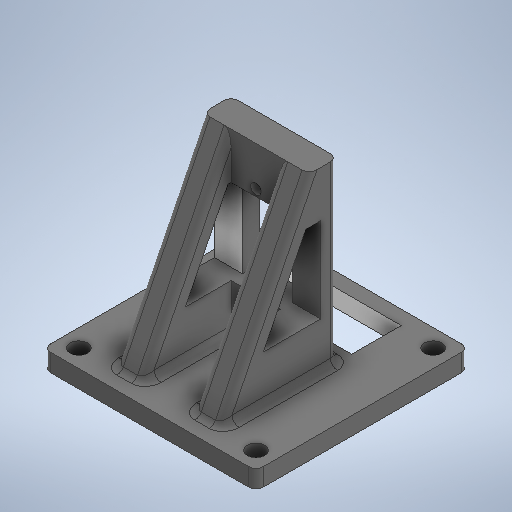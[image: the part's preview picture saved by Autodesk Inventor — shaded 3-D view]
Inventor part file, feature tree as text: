
AUTODESK INVENTOR PART (.ipt)
format: ipt  version: 2025.2 (Build 292293000, 293)  size: 428,032 bytes
history: native  units: mm
features: sketch x13, extrude x7, hole x3, fillet x3, other x1
ambient origin geometry x8: Origin, YZ Plane, XZ Plane, XY Plane, X Axis, Y Axis, Z Axis, Center Point
bodies: Body1 (feature_tree)
feature tree (27):
  other  "Bryła1"
  extrude  "Wyciągnięcie proste1"  Depth=60.0mm
  hole  "Otwór1"  [1 undecoded]
  fillet  "Zaokrąglenie1"  Radius=5.0mm
  extrude  "Wyciągnięcie proste2"  Depth=50.0mm
  sketch  "Szkic8"
  extrude  "Wyciągnięcie proste3"  Depth=50.0mm
  sketch  "Szkic10"
  hole  "Otwór2"  [1 undecoded]
  hole  "Otwór3"  [1 undecoded]
  extrude  "Wyciągnięcie proste4"  Depth=7.0mm
  extrude  "Wyciągnięcie proste5"  Depth=8.0mm
  fillet  "Zaokrąglenie2"  Radius=25.0mm
  sketch  "Szkic15"
  extrude  "Wyciągnięcie proste6"  Depth=8.0mm
  fillet  "Zaokrąglenie3"  Radius=25.0mm
  extrude  "Wyciągnięcie proste7"  Depth=30.0mm
  sketch  "Szkic1"
  sketch  "Szkic2"
  sketch  "Szkic5"
  sketch  "Szkic9"
  sketch  "Szkic11"
  sketch  "Szkic12"
  sketch  "Szkic13"
  sketch  "Szkic14"
  sketch  "Szkic16"
  sketch  "Szkic17"
note: 3 required parameter values undecoded (feature->parameter linkage not recoverable at this tier; creation-order binding heuristic only, values carry confidence <= 0.55)
